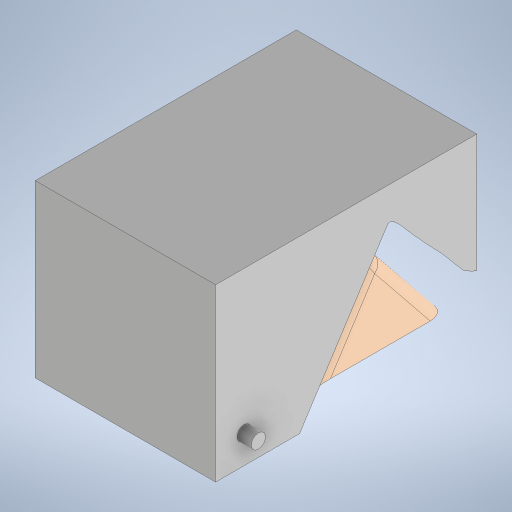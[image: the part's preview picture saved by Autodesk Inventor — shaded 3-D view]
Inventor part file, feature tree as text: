
AUTODESK INVENTOR PART (.ipt)
format: ipt  version: 2024 (Build 280153000, 153)  size: 10,908,672 bytes
history: native  units: mm
features: other x6, extrude x5, sketch x5, plane x2
ambient origin geometry x8: Origin, YZ Plane, XZ Plane, XY Plane, X Axis, Y Axis, Z Axis, Center Point
bodies: Body1 (feature_tree)
feature tree (18):
  other  "M.ipt"
  plane  "Plano de trabajo1"
  extrude  "Extrusión1"  [1 undecoded]
  other  "Combinar1"
  sketch  "Boceto3"  dims[d2=550.0mm d3=520.0mm]
  sketch  "Boceto4"  dims[d4=550.0mm d5=0.0mm d6=129.8482mm]
  plane  "Plano de trabajo2"
  sketch  "Boceto5"  dims[d17=180.0mm d18=180.0mm]
  extrude  "Extrusión2"  Depth=520.0mm
  extrude  "Extrusión3"  Depth=129.8482mm
  extrude  "Extrusión4"  Depth=180.0mm
  extrude  "Extrusión5"  Depth=205.0mm
  other  "Sólido1::M.ipt"
  other  "OperaciónIdentificador1"
  sketch  "Boceto1"  dims[d0=25.0mm d1=-365.0mm]
  other  "Sólido2"
  sketch  "Boceto6"  dims[d22=326.0mm d23=180.0mm d24=180.0mm d25=180.0mm d26=10.0mm d27=0.0mm d28=1000.0mm d29=0.0mm d30=1000.0mm d31=0.0mm d32=30.0mm d33=30.0mm d34=15.0mm d35=15.0mm d36=205.0mm d37=0.0mm d38=0.0mm d14=0.5mm d15=0.872665mm d16=0.5mm d19=0.5mm d20=0.872665mm d21=0.5mm]
  other  "Sólido1"
note: 1 required parameter value undecoded (feature->parameter linkage not recoverable at this tier; creation-order binding heuristic only, values carry confidence <= 0.55)
